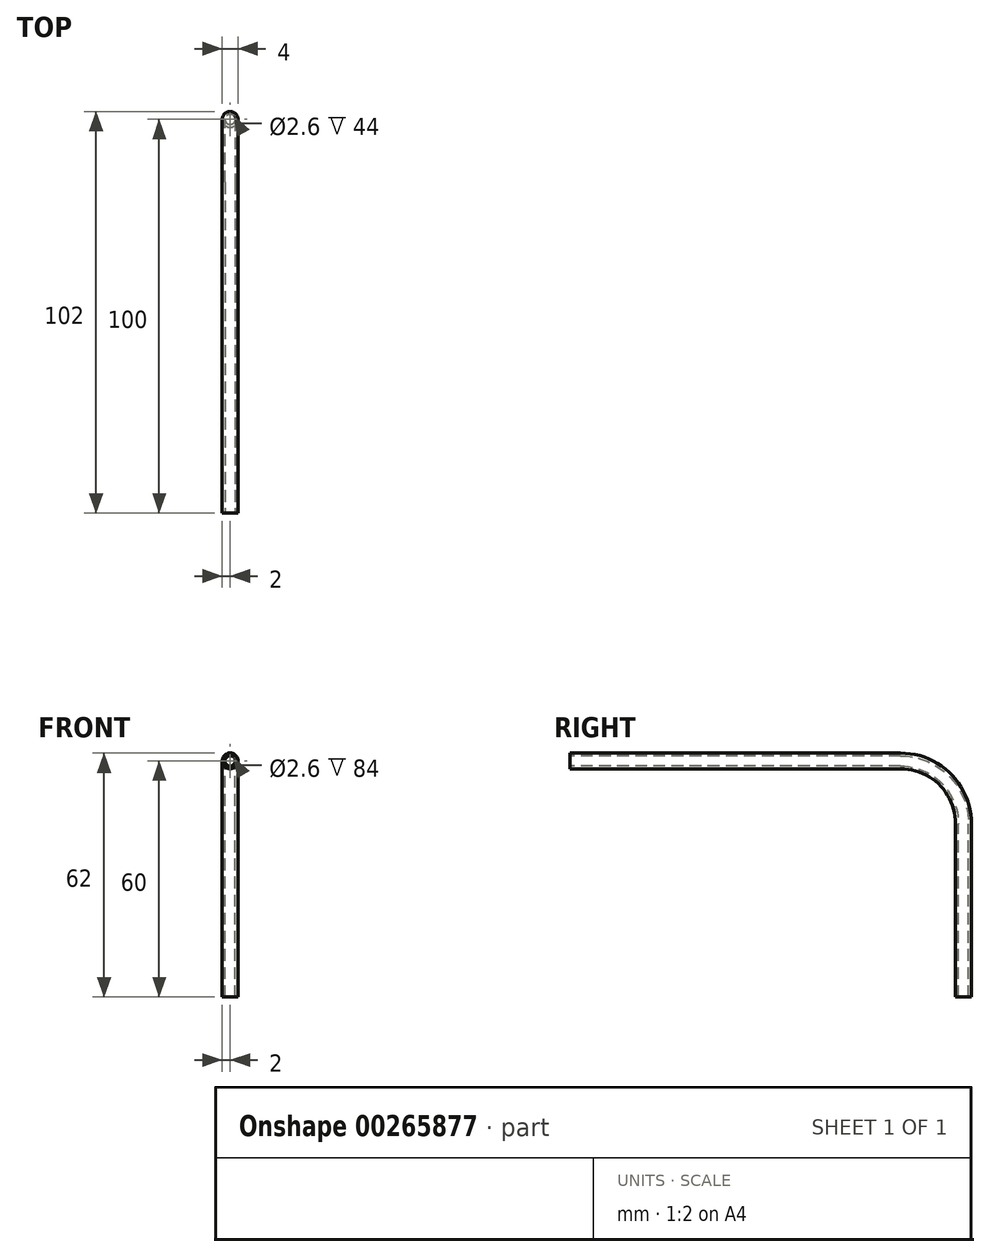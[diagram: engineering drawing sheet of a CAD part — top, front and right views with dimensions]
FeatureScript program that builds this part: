
annotation { "Feature Type Name" : "Feature", "Feature Type Description" : "" }
export const myFeature = defineFeature(function(context is Context, id is Id, definition is map)
    precondition{}
    {
        {
            var Q0;
            Q0=qCreatedBy(makeId("Top.planeOp"),FACE);
            var sketch = newSketch(context, id + "F0", { "sketchPlane" : qUnion([Q0])});
            skCircle(sketch, "E0", {"center": v(0, 0) * mm, "radius": 2 * mm});
            skCircle(sketch, "E1", {"center": v(0, 0) * mm, "radius": 1.3 * mm});
            skSolve(sketch);
        }
        {
            var Q0;
            Q0=qCreatedBy(makeId("Right.planeOp"),FACE);
            var sketch = newSketch(context, id + "F1", { "sketchPlane" : qUnion([Q0])});
            skLineSegment(sketch, "E2", {"start": v(0, 0) * mm, "end": v(0, 44) * mm});
            skLineSegment(sketch, "E3", {"start": v(-16, 60) * mm, "end": v(-100, 60) * mm});
            skPoint(sketch, "E4.visualSharp", {"position": v(0, 60) * mm});
            skArc(sketch, "E4.filletArc", {"start": v(0, 44) * mm, "mid": v(-4.69, 55.31) * mm, "end": v(-16, 60) * mm});
            skSolve(sketch);
        }
        {
            var Q0;
            Q0 = qSketchRegion(id + "F0", true);
            var Q1;
            Q1 = qConstructionFilter(qBodyType(qCreatedBy(id + "F1" ,EDGE), BodyType.WIRE), ConstructionObject.NO);
            sweep(context, id + "F2", {"profiles" : qUnion([Q0]), "path" : qUnion([Q1])});
        }
    });
